# Revit family: Indoor_Pendant Lamp_Santa&Cole_Lámina 85
name_source: partatom
category: Luminarias
revit_build: Autodesk Revit 2018 (Build: 20190510_1515(x64)
units: mm (PartAtom-declared; Revit-internal decimal feet)

## family parameters
Anfitrión = Cara
Compartido = No
Corte con vacíos al cargar = No
Cota de conector redondo = Diámetro de uso
Origen de luz = Sí
Punto de cálculo de habitación = No
Tipo de pieza = Normal

## types (1)
- Lámina 85
    Anchura rectángulo de emisión = 841 mm
    Archivo de red fotométrica = LAM851 (CL004A19F007G).IES
    Assembly Instructions - CE = https://www.santacole.com
    Assembly Instructions - UL = https://www.santacole.com
    Cambio de temperatura de color de luz atenuada = <Ninguno>
    Carga aparente = 31 W
    Code = LAM851
    Elevación por defecto = 1219 mm
    Energy Label = https://www.santacole.com
    Fabricante = Santa & Cole
    Filtro de color = 16777215
    Forma visible en renderización = No
    Load = 31 W
    Longitud de rectángulo de emisión = 19 mm  [stored 0.062336 ft]
    Manufacturer website = http://www.santacole.com
    Modelo = Lámina
    Technical Information = https://www.santacole.com
    URL = https://www.santacole.com
    Voltaje (90-305 V) = 220 V
    Ángulo de inclinación = 90.00°

note: [stored X ft] marks values corroborated as IEEE doubles in the binary element streams (Revit-internal decimal feet)

## geometry (parser evidence)
native form markers: Blend x4, Sweep x2
no freeform markers — native parametric forms only
